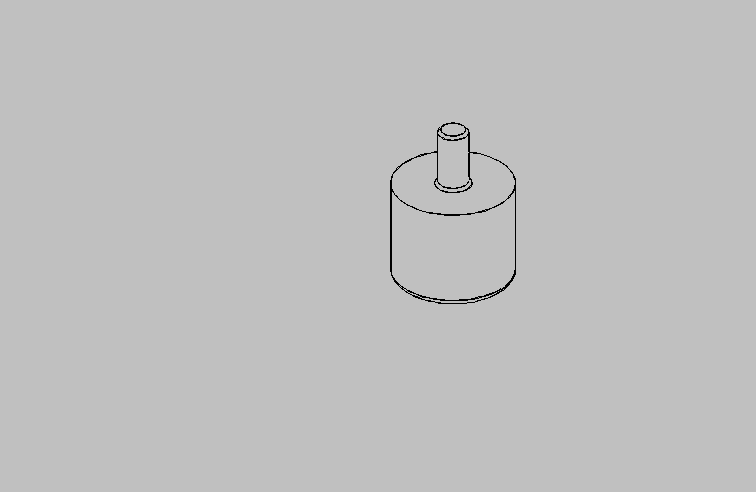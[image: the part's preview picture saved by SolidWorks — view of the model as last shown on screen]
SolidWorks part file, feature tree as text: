
SOLIDWORKS PART (.sldprt)
format: sldprt  version: not decoded by parser v0  size: 104,960 bytes
history: native  units: mm
features: plane x3, sketch x2, chamfer x2, material x1, revolve x1, extrude x1, fillet x1 (+9 scaffold rows collapsed)
feature tree (20):
  scaffold x9  (default folders/planes/origin — collapsed)
  material  "Material <not specified>"
  plane  "Face"
  plane  "Dessus"
  plane  "Droite"
  sketch  "Esquisse1"  dims[c1.D2=6.25mm c1.D1=10.0mm c2.D2=10.0mm c2.D3=6.25mm c2.D4=20.0mm c3.D3=6.25mm c3.D4=20.0mm c3.D5=3.0mm]
  revolve  "Révolution1"  Angle=360deg
  sketch  "Esquisse2"  dims[D1=5.0mm]
  extrude  "Extrusion1"  Depth=10mm
  fillet  "Congé1"  Radius=1mm
  chamfer  "Chanfrein1"  Distance=0.5mm Angle=45deg
  chamfer  "Congé2"  Distance=0.5mm
decode coverage: 7 of 7 modeling features carry decoded parameters
note: suppression state not decoded; provenance and decode notes live in map.json
